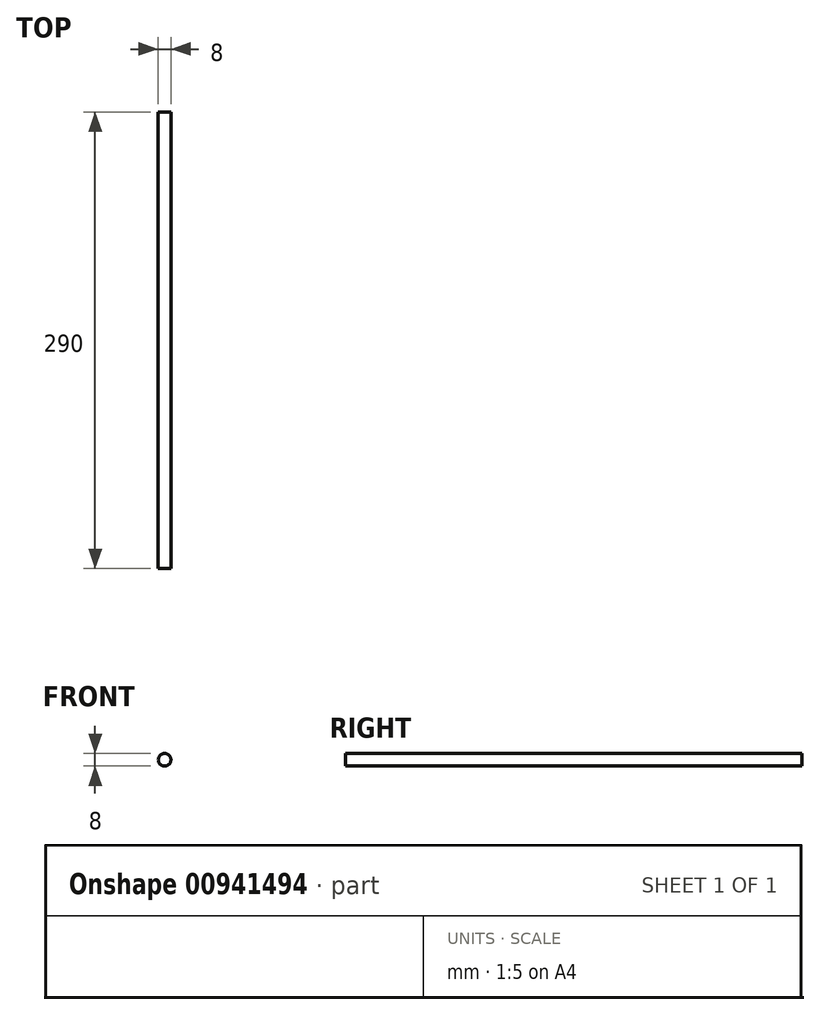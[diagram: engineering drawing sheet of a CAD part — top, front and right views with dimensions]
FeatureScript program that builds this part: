
annotation { "Feature Type Name" : "Feature", "Feature Type Description" : "" }
export const myFeature = defineFeature(function(context is Context, id is Id, definition is map)
    precondition{}
    {
        {
            var Q0;
            Q0=qCreatedBy(makeId("Front.planeOp"),FACE);
            var sketch = newSketch(context, id + "F0", { "sketchPlane" : qUnion([Q0])});
            skCircle(sketch, "E0", {"center": v(0, 0) * mm, "radius": 4 * mm});
            skSolve(sketch);
        }
        {
            var Q0;
            Q0=makeQuery(id+"F0.imprint","IMPRINT",FACE,{"disambiguationData":[TD([[makeQuery(id+"F0.imprint","IMPRINT",EDGE,{"derivedFrom":sQuery(id+"F0.wireOp",EDGE,"E0")}),1.0]])]});
            extrude(context, id + "F1", {"entities" : qUnion([Q0]), "depth" : 290 * mm, "offsetDistance" : 25 * mm});
        }
    });
